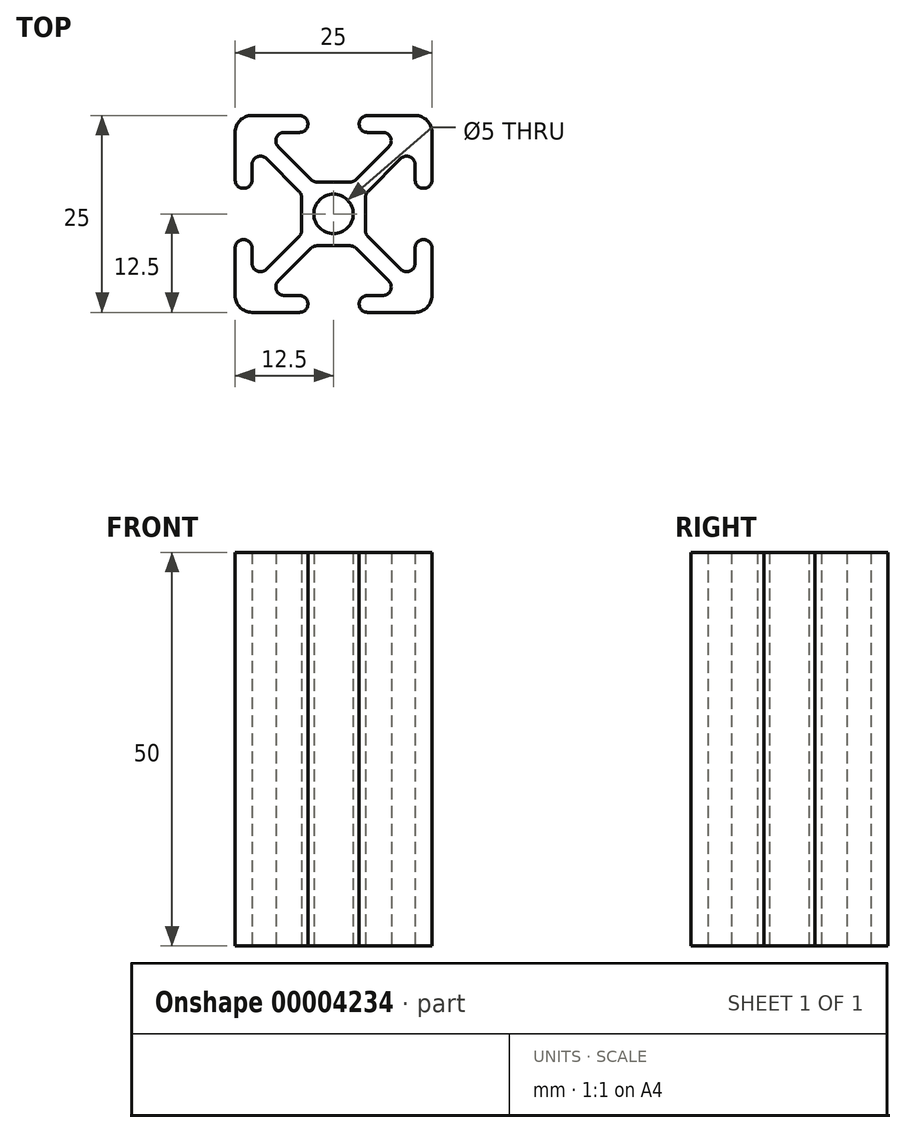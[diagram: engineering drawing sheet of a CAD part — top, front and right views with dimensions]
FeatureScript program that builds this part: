
annotation { "Feature Type Name" : "Feature", "Feature Type Description" : "" }
export const myFeature = defineFeature(function(context is Context, id is Id, definition is map)
    precondition{}
    {
        {
            var Q0;
            Q0=qCreatedBy(makeId("Top.planeOp"),FACE);
            var sketch = newSketch(context, id + "F0", { "sketchPlane" : qUnion([Q0])});
            skCircle(sketch, "E0", {"center": v(0, 0) * mm, "radius": 2.5 * mm});
            skLineSegment(sketch, "E1", {"start": v(0, 0) * mm, "end": v(0, 4.05) * mm, "construction": true});
            skLineSegment(sketch, "E2", {"start": v(0, 0) * mm, "end": v(-4.05, 0) * mm, "construction": true});
            skLineSegment(sketch, "E3", {"start": v(0, 0) * mm, "end": v(-12.5, 12.5) * mm, "construction": true});
            skLineSegment(sketch, "E4", {"start": v(-12.5, 10.36) * mm, "end": v(-12.5, 4.32) * mm});
            skLineSegment(sketch, "E5", {"start": v(-10.36, 12.5) * mm, "end": v(-4.32, 12.5) * mm});
            skLineSegment(sketch, "E6", {"start": v(-4.32, 10.36) * mm, "end": v(-6.26, 10.36) * mm});
            skLineSegment(sketch, "E7", {"start": v(-10.36, 6.26) * mm, "end": v(-10.36, 4.32) * mm});
            skArc(sketch, "E8", {"start": v(-4.32, 12.5) * mm, "mid": v(-3.25, 11.43) * mm, "end": v(-4.32, 10.36) * mm});
            skArc(sketch, "E9", {"start": v(-10.36, 4.32) * mm, "mid": v(-11.43, 3.25) * mm, "end": v(-12.5, 4.32) * mm});
            skLineSegment(sketch, "E10", {"start": v(0, 4.05) * mm, "end": v(-2.1, 4.05) * mm});
            skLineSegment(sketch, "E11", {"start": v(-4.05, 2.1) * mm, "end": v(-4.05, 0) * mm});
            skLineSegment(sketch, "E12", {"start": v(-8.53, 7.02) * mm, "end": v(-4.36, 2.85) * mm});
            skLineSegment(sketch, "E13", {"start": v(-7.02, 8.53) * mm, "end": v(-2.85, 4.36) * mm});
            skLineSegment(sketch, "E14.0.MirrorCS", {"start": v(10.36, 6.26) * mm, "end": v(10.36, 4.32) * mm});
            skLineSegment(sketch, "E14.1.MirrorCS", {"start": v(7.02, 8.53) * mm, "end": v(2.85, 4.36) * mm});
            skArc(sketch, "E14.2.MirrorCS", {"start": v(4.32, 12.5) * mm, "mid": v(3.25, 11.43) * mm, "end": v(4.32, 10.36) * mm});
            skArc(sketch, "E14.3.MirrorCS", {"start": v(10.36, 4.32) * mm, "mid": v(11.43, 3.25) * mm, "end": v(12.5, 4.32) * mm});
            skLineSegment(sketch, "E14.4.MirrorCS", {"start": v(10.36, 12.5) * mm, "end": v(4.32, 12.5) * mm});
            skLineSegment(sketch, "E14.5.MirrorCS", {"start": v(4.32, 10.36) * mm, "end": v(6.26, 10.36) * mm});
            skLineSegment(sketch, "E14.6.MirrorCS", {"start": v(12.5, 10.36) * mm, "end": v(12.5, 4.32) * mm});
            skLineSegment(sketch, "E14.7.MirrorCS", {"start": v(8.53, 7.02) * mm, "end": v(4.36, 2.85) * mm});
            skLineSegment(sketch, "E15.0.MirrorCS", {"start": v(0, 4.05) * mm, "end": v(2.1, 4.05) * mm});
            skLineSegment(sketch, "E16.0.MirrorCS", {"start": v(4.05, 2.1) * mm, "end": v(4.05, 0) * mm});
            skLineSegment(sketch, "E17.0.MirrorCS", {"start": v(10.36, -12.5) * mm, "end": v(4.32, -12.5) * mm});
            skLineSegment(sketch, "E17.1.MirrorCS", {"start": v(12.5, -10.36) * mm, "end": v(12.5, -4.32) * mm});
            skArc(sketch, "E17.2.MirrorCS", {"start": v(4.32, -12.5) * mm, "mid": v(3.25, -11.43) * mm, "end": v(4.32, -10.36) * mm});
            skLineSegment(sketch, "E17.3.MirrorCS", {"start": v(-7.02, -8.53) * mm, "end": v(-2.85, -4.36) * mm});
            skLineSegment(sketch, "E17.4.MirrorCS", {"start": v(7.02, -8.53) * mm, "end": v(2.85, -4.36) * mm});
            skLineSegment(sketch, "E17.5.MirrorCS", {"start": v(10.36, -6.26) * mm, "end": v(10.36, -4.32) * mm});
            skLineSegment(sketch, "E17.6.MirrorCS", {"start": v(8.53, -7.02) * mm, "end": v(4.36, -2.85) * mm});
            skLineSegment(sketch, "E17.7.MirrorCS", {"start": v(-10.36, -12.5) * mm, "end": v(-4.32, -12.5) * mm});
            skLineSegment(sketch, "E17.8.MirrorCS", {"start": v(-4.32, -10.36) * mm, "end": v(-6.26, -10.36) * mm});
            skLineSegment(sketch, "E17.9.MirrorCS", {"start": v(4.32, -10.36) * mm, "end": v(6.26, -10.36) * mm});
            skArc(sketch, "E17.10.MirrorCS", {"start": v(10.36, -4.32) * mm, "mid": v(11.43, -3.25) * mm, "end": v(12.5, -4.32) * mm});
            skLineSegment(sketch, "E17.11.MirrorCS", {"start": v(-12.5, -10.36) * mm, "end": v(-12.5, -4.32) * mm});
            skLineSegment(sketch, "E17.12.MirrorCS", {"start": v(0, -4.05) * mm, "end": v(2.1, -4.05) * mm});
            skArc(sketch, "E17.13.MirrorCS", {"start": v(-4.32, -12.5) * mm, "mid": v(-3.25, -11.43) * mm, "end": v(-4.32, -10.36) * mm});
            skLineSegment(sketch, "E17.14.MirrorCS", {"start": v(-8.53, -7.02) * mm, "end": v(-4.36, -2.85) * mm});
            skArc(sketch, "E17.15.MirrorCS", {"start": v(-10.36, -4.32) * mm, "mid": v(-11.43, -3.25) * mm, "end": v(-12.5, -4.32) * mm});
            skLineSegment(sketch, "E17.16.MirrorCS", {"start": v(-10.36, -6.26) * mm, "end": v(-10.36, -4.32) * mm});
            skLineSegment(sketch, "E17.17.MirrorCS", {"start": v(0, -4.05) * mm, "end": v(-2.1, -4.05) * mm});
            skLineSegment(sketch, "E18.0.MirrorCS", {"start": v(4.05, -2.1) * mm, "end": v(4.05, 0) * mm});
            skLineSegment(sketch, "E19.0.MirrorCS", {"start": v(-4.05, -2.1) * mm, "end": v(-4.05, 0) * mm});
            skPoint(sketch, "E20.visualSharp", {"position": v(-12.5, 12.5) * mm});
            skArc(sketch, "E20.filletArc", {"start": v(-10.36, 12.5) * mm, "mid": v(-11.87, 11.87) * mm, "end": v(-12.5, 10.36) * mm});
            skPoint(sketch, "E21.visualSharp", {"position": v(12.5, 12.5) * mm});
            skArc(sketch, "E21.filletArc", {"start": v(12.5, 10.36) * mm, "mid": v(11.87, 11.87) * mm, "end": v(10.36, 12.5) * mm});
            skPoint(sketch, "E22.visualSharp", {"position": v(12.5, -12.5) * mm});
            skArc(sketch, "E22.filletArc", {"start": v(10.36, -12.5) * mm, "mid": v(11.87, -11.87) * mm, "end": v(12.5, -10.36) * mm});
            skPoint(sketch, "E23.visualSharp", {"position": v(-12.5, -12.5) * mm});
            skArc(sketch, "E23.filletArc", {"start": v(-12.5, -10.36) * mm, "mid": v(-11.87, -11.87) * mm, "end": v(-10.36, -12.5) * mm});
            skPoint(sketch, "E24.visualSharp", {"position": v(4.05, 4.05) * mm});
            skPoint(sketch, "E25.visualSharp", {"position": v(-10.36, 8.85) * mm});
            skArc(sketch, "E25.filletArc", {"start": v(-8.53, 7.02) * mm, "mid": v(-9.7, 7.25) * mm, "end": v(-10.36, 6.26) * mm});
            skPoint(sketch, "E26.visualSharp", {"position": v(-8.85, 10.36) * mm});
            skArc(sketch, "E26.filletArc", {"start": v(-6.26, 10.36) * mm, "mid": v(-7.25, 9.7) * mm, "end": v(-7.02, 8.53) * mm});
            skPoint(sketch, "E27.visualSharp", {"position": v(8.85, 10.36) * mm});
            skArc(sketch, "E27.filletArc", {"start": v(7.02, 8.53) * mm, "mid": v(7.25, 9.7) * mm, "end": v(6.26, 10.36) * mm});
            skPoint(sketch, "E28.visualSharp", {"position": v(10.36, 8.85) * mm});
            skArc(sketch, "E28.filletArc", {"start": v(10.36, 6.26) * mm, "mid": v(9.7, 7.25) * mm, "end": v(8.53, 7.02) * mm});
            skPoint(sketch, "E29.visualSharp", {"position": v(10.36, -8.85) * mm});
            skArc(sketch, "E29.filletArc", {"start": v(8.53, -7.02) * mm, "mid": v(9.7, -7.25) * mm, "end": v(10.36, -6.26) * mm});
            skPoint(sketch, "E30.visualSharp", {"position": v(8.85, -10.36) * mm});
            skArc(sketch, "E30.filletArc", {"start": v(6.26, -10.36) * mm, "mid": v(7.25, -9.7) * mm, "end": v(7.02, -8.53) * mm});
            skPoint(sketch, "E31.visualSharp", {"position": v(-8.85, -10.36) * mm});
            skArc(sketch, "E31.filletArc", {"start": v(-7.02, -8.53) * mm, "mid": v(-7.25, -9.7) * mm, "end": v(-6.26, -10.36) * mm});
            skPoint(sketch, "E32.visualSharp", {"position": v(-10.36, -8.85) * mm});
            skArc(sketch, "E32.filletArc", {"start": v(-10.36, -6.26) * mm, "mid": v(-9.7, -7.25) * mm, "end": v(-8.53, -7.02) * mm});
            skPoint(sketch, "E33.orphan", {"position": v(-4.05, 4.05) * mm});
            skPoint(sketch, "E34.orphan", {"position": v(4.05, -4.05) * mm});
            skPoint(sketch, "E35.orphan", {"position": v(-4.05, -4.05) * mm});
            skPoint(sketch, "E36.visualSharp", {"position": v(-2.54, 4.05) * mm});
            skArc(sketch, "E36.filletArc", {"start": v(-2.85, 4.36) * mm, "mid": v(-2.5, 4.13) * mm, "end": v(-2.1, 4.05) * mm});
            skPoint(sketch, "E37.visualSharp", {"position": v(2.54, 4.05) * mm});
            skArc(sketch, "E37.filletArc", {"start": v(2.1, 4.05) * mm, "mid": v(2.5, 4.13) * mm, "end": v(2.85, 4.36) * mm});
            skPoint(sketch, "E38.visualSharp", {"position": v(-4.05, 2.54) * mm});
            skArc(sketch, "E38.filletArc", {"start": v(-4.05, 2.1) * mm, "mid": v(-4.13, 2.5) * mm, "end": v(-4.36, 2.85) * mm});
            skPoint(sketch, "E39.visualSharp", {"position": v(-4.05, -2.54) * mm});
            skArc(sketch, "E39.filletArc", {"start": v(-4.36, -2.85) * mm, "mid": v(-4.13, -2.5) * mm, "end": v(-4.05, -2.1) * mm});
            skPoint(sketch, "E40.visualSharp", {"position": v(-2.54, -4.05) * mm});
            skArc(sketch, "E40.filletArc", {"start": v(-2.1, -4.05) * mm, "mid": v(-2.5, -4.13) * mm, "end": v(-2.85, -4.36) * mm});
            skPoint(sketch, "E41.visualSharp", {"position": v(2.54, -4.05) * mm});
            skArc(sketch, "E41.filletArc", {"start": v(2.85, -4.36) * mm, "mid": v(2.5, -4.13) * mm, "end": v(2.1, -4.05) * mm});
            skPoint(sketch, "E42.visualSharp", {"position": v(4.05, -2.54) * mm});
            skArc(sketch, "E42.filletArc", {"start": v(4.05, -2.1) * mm, "mid": v(4.13, -2.5) * mm, "end": v(4.36, -2.85) * mm});
            skPoint(sketch, "E43.visualSharp", {"position": v(4.05, 2.54) * mm});
            skArc(sketch, "E43.filletArc", {"start": v(4.36, 2.85) * mm, "mid": v(4.13, 2.5) * mm, "end": v(4.05, 2.1) * mm});
            skSolve(sketch);
        }
        {
            var Q0;
            Q0=makeQuery(id+"F0.imprint","IMPRINT",FACE,{"disambiguationData":[TD([[makeQuery(id+"F0.imprint","IMPRINT",EDGE,{"derivedFrom":sQuery(id+"F0.wireOp",EDGE,"E0")}),-1.0]])]});
            extrude(context, id + "F1", {"entities" : qUnion([Q0]), "depth" : 50 * mm});
        }
    });
